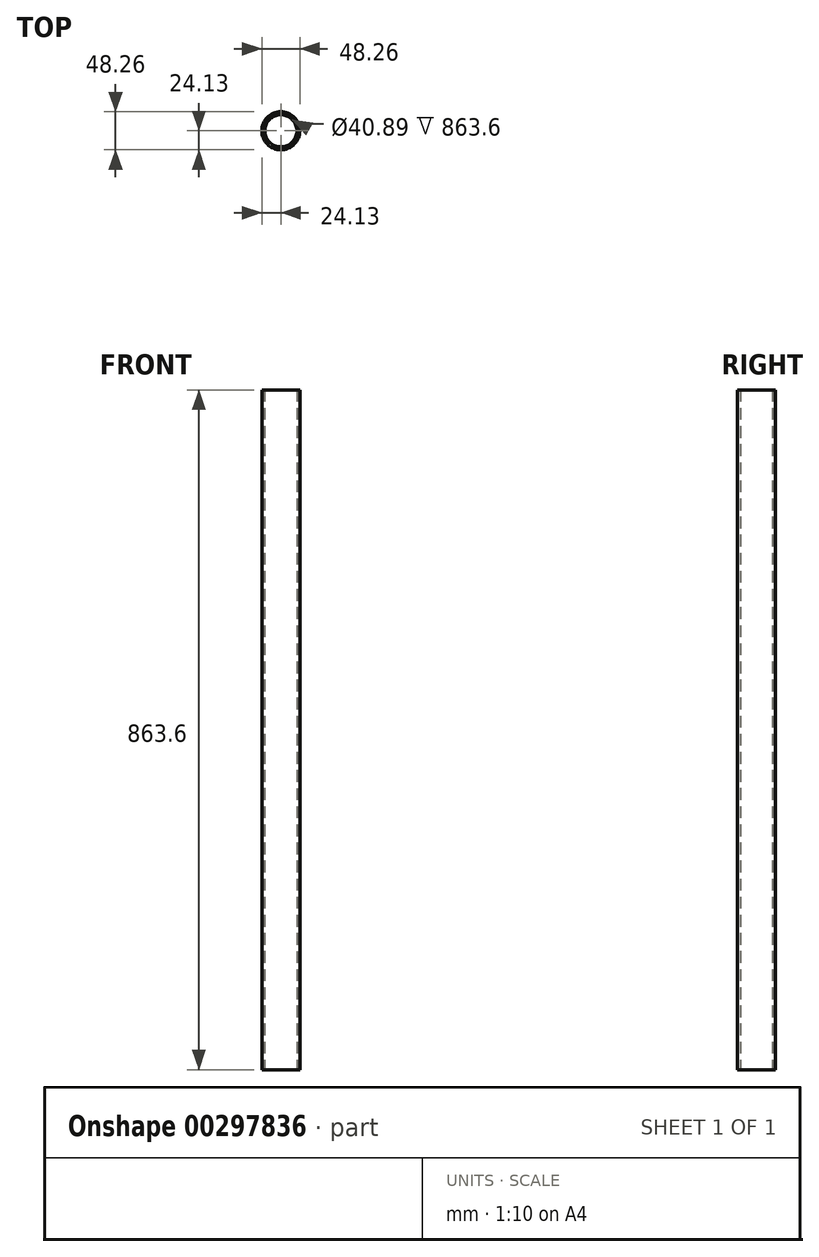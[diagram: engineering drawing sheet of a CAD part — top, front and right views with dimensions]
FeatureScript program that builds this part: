
annotation { "Feature Type Name" : "Feature", "Feature Type Description" : "" }
export const myFeature = defineFeature(function(context is Context, id is Id, definition is map)
    precondition{}
    {
        {
            var Q0;
            Q0=qCreatedBy(makeId("Top.planeOp"),FACE);
            var sketch = newSketch(context, id + "F0", { "sketchPlane" : qUnion([Q0])});
            skCircle(sketch, "E0", {"center": v(0, 0) * mm, "radius": 24.13 * mm});
            skCircle(sketch, "E1", {"center": v(0, 0) * mm, "radius": 20.45 * mm});
            skSolve(sketch);
        }
        {
            var Q0;
            Q0=makeQuery(id+"F0.imprint","IMPRINT",FACE,{"disambiguationData":[TD([[makeQuery(id+"F0.imprint","IMPRINT",EDGE,{"derivedFrom":sQuery(id+"F0.wireOp",EDGE,"E0")}),1.0]])]});
            extrude(context, id + "F1", {"entities" : qUnion([Q0]), "depth" : 863.6 * mm});
        }
    });
